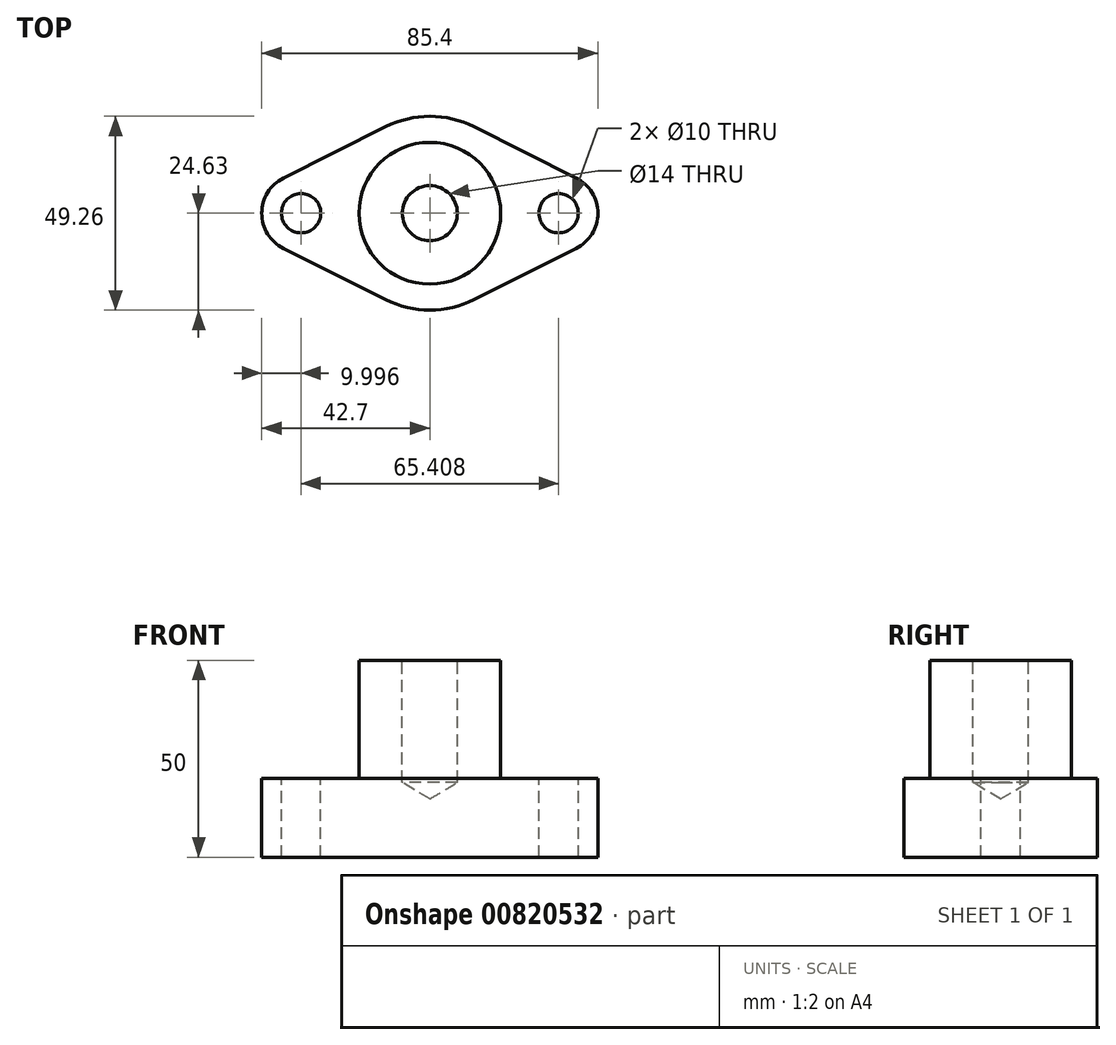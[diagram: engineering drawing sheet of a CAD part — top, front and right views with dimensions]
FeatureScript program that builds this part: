
annotation { "Feature Type Name" : "Feature", "Feature Type Description" : "" }
export const myFeature = defineFeature(function(context is Context, id is Id, definition is map)
    precondition{}
    {
        {
            var Q0;
            Q0=qCreatedBy(makeId("Top.planeOp"),FACE);
            var sketch = newSketch(context, id + "F0", { "sketchPlane" : qUnion([Q0])});
            skLineSegment(sketch, "E0", {"start": v(-55, 0) * mm, "end": v(0, 27.6) * mm});
            skLineSegment(sketch, "E1", {"start": v(0, 27.6) * mm, "end": v(55, 0) * mm});
            skLineSegment(sketch, "E2", {"start": v(55, 0) * mm, "end": v(0, -27.6) * mm});
            skLineSegment(sketch, "E3", {"start": v(0, -27.6) * mm, "end": v(-55, 0) * mm});
            skSolve(sketch);
        }
        {
            var Q0;
            Q0=makeQuery(id+"F0.imprint","IMPRINT",FACE,{"disambiguationData":[TD([[makeQuery(id+"F0.imprint","IMPRINT",EDGE,{"derivedFrom":sQuery(id+"F0.wireOp",EDGE,"E0")}),-1.0]])]});
            extrude(context, id + "F1", {"entities" : qUnion([Q0]), "depth" : 20 * mm, "offsetDistance" : 25 * mm});
        }
        {
            var Q0;
            Q0=makeQuery(id+"F1.opExtrude","SWEPT_EDGE",EDGE,{"disambiguationData":[OSD([sQuery(id+"F0.wireOp",EDGE,"E1"),sQuery(id+"F0.wireOp",EDGE,"E2")])]});
            var Q1;
            Q1=makeQuery(id+"F1.opExtrude","SWEPT_EDGE",EDGE,{"disambiguationData":[OSD([sQuery(id+"F0.wireOp",EDGE,"E0"),sQuery(id+"F0.wireOp",EDGE,"E3")])]});
            fillet(context, id + "F2", {"entities" : qUnion([Q0, Q1]), "radius" : 10 * mm, "tangentPropagation" : true, "allowEdgeOverflow" : false});
        }
        {
            var Q0;
            Q0=makeQuery(id+"F1.opExtrude","SWEPT_EDGE",EDGE,{"disambiguationData":[OSD([sQuery(id+"F0.wireOp",EDGE,"E0"),sQuery(id+"F0.wireOp",EDGE,"E1")])]});
            var Q1;
            Q1=makeQuery(id+"F1.opExtrude","SWEPT_EDGE",EDGE,{"disambiguationData":[OSD([sQuery(id+"F0.wireOp",EDGE,"E2"),sQuery(id+"F0.wireOp",EDGE,"E3")])]});
            fillet(context, id + "F3", {"entities" : qUnion([Q0, Q1]), "radius" : 25 * mm, "tangentPropagation" : true, "allowEdgeOverflow" : false});
        }
        {
            var Q0;
            Q0=makeQuery(id+"F1.opExtrude","CAP_FACE",FACE,{"disambiguationData":[OSD([sQuery(id+"F0.wireOp",EDGE,"E0"),sQuery(id+"F0.wireOp",EDGE,"E1"),sQuery(id+"F0.wireOp",EDGE,"E2"),sQuery(id+"F0.wireOp",EDGE,"E3")])],"isStart":false});
            var sketch = newSketch(context, id + "F4", { "sketchPlane" : qUnion([Q0])});
            skPoint(sketch, "E4", {"position": v(-32.7, 0) * mm});
            skPoint(sketch, "E5", {"position": v(32.7, 0) * mm});
            skCircle(sketch, "E6", {"center": v(0, 0) * mm, "radius": 18 * mm});
            skSolve(sketch);
        }
        {
            var Q0;
            Q0=sQuery(id+"F4.wireOp",VERTEX,"E4");
            var Q1;
            Q1=sQuery(id+"F4.wireOp",VERTEX,"E5");
            var Q2;
            Q2=makeQuery(id+"F1.opExtrude","SWEPT_BODY",BODY,{"disambiguationData":[OSD([sQuery(id+"F0.wireOp",EDGE,"E0"),sQuery(id+"F0.wireOp",EDGE,"E1"),sQuery(id+"F0.wireOp",EDGE,"E2"),sQuery(id+"F0.wireOp",EDGE,"E3")])]});
            hole(context, id + "F5", {"style" : HoleStyle.SIMPLE, "endStyle" : HoleEndStyle.THROUGH, "holeDiameter" : 10 * mm, "majorDiameter" : 5 * mm, "isTappedThrough" : true, "tappedDepth" : 12 * mm, "tapClearance" : 3, "locations" : qUnion([Q0, Q1]), "scope" : qUnion([Q2])});
        }
        {
            var Q0;
            Q0=makeQuery(id+"F1.opExtrude","CAP_FACE",FACE,{"disambiguationData":[OSD([sQuery(id+"F0.wireOp",EDGE,"E0"),sQuery(id+"F0.wireOp",EDGE,"E1"),sQuery(id+"F0.wireOp",EDGE,"E2"),sQuery(id+"F0.wireOp",EDGE,"E3")])],"isStart":false});
            var sketch = newSketch(context, id + "F6", { "sketchPlane" : qUnion([Q0])});
            skCircle(sketch, "E7", {"center": v(0, 0) * mm, "radius": 18 * mm});
            skSolve(sketch);
        }
        {
            var Q0;
            Q0 = qSketchRegion(id + "F6", true);
            extrude(context, id + "F7", {"entities" : qUnion([Q0]), "operationType" : NewBodyOperationType.ADD, "depth" : 30 * mm, "offsetDistance" : 25 * mm});
        }
        {
            var Q0;
            Q0=makeQuery(id+"F7.opExtrude","CAP_FACE",FACE,{"disambiguationData":[OSD([sQuery(id+"F6.wireOp",EDGE,"E7")])],"isStart":false});
            var sketch = newSketch(context, id + "F8", { "sketchPlane" : qUnion([Q0])});
            skPoint(sketch, "E8", {"position": v(0, 0) * mm});
            skSolve(sketch);
        }
        {
            var Q0;
            Q0=sQuery(id+"F8.wireOp",VERTEX,"E8");
            var Q1;
            Q1=makeQuery(id+"F1.opExtrude","SWEPT_BODY",BODY,{"disambiguationData":[OSD([sQuery(id+"F0.wireOp",EDGE,"E0"),sQuery(id+"F0.wireOp",EDGE,"E1"),sQuery(id+"F0.wireOp",EDGE,"E2"),sQuery(id+"F0.wireOp",EDGE,"E3")])]});
            hole(context, id + "F9", {"style" : HoleStyle.SIMPLE, "endStyle" : HoleEndStyle.BLIND, "standardTappedOrClearance" : lookupTablePath({ "standard" : "ISO", "engagement" : "75%", "pitch" : "2 mm", "size" : "M16", "type" : "Tapped" }), "standardBlindInLast" : lookupTablePath({ "standard" : "ISO", "engagement" : "75%", "pitch" : "2 mm", "size" : "M16", "type" : "Tapped" }), "holeDiameter" : 14 * mm, "majorDiameter" : 16 * mm, "showTappedDepth" : true, "holeDepth" : 31 * mm, "isTappedThrough" : true, "tappedDepth" : 25 * mm, "tapClearance" : 3, "locations" : qUnion([Q0]), "scope" : qUnion([Q1])});
        }
    });
